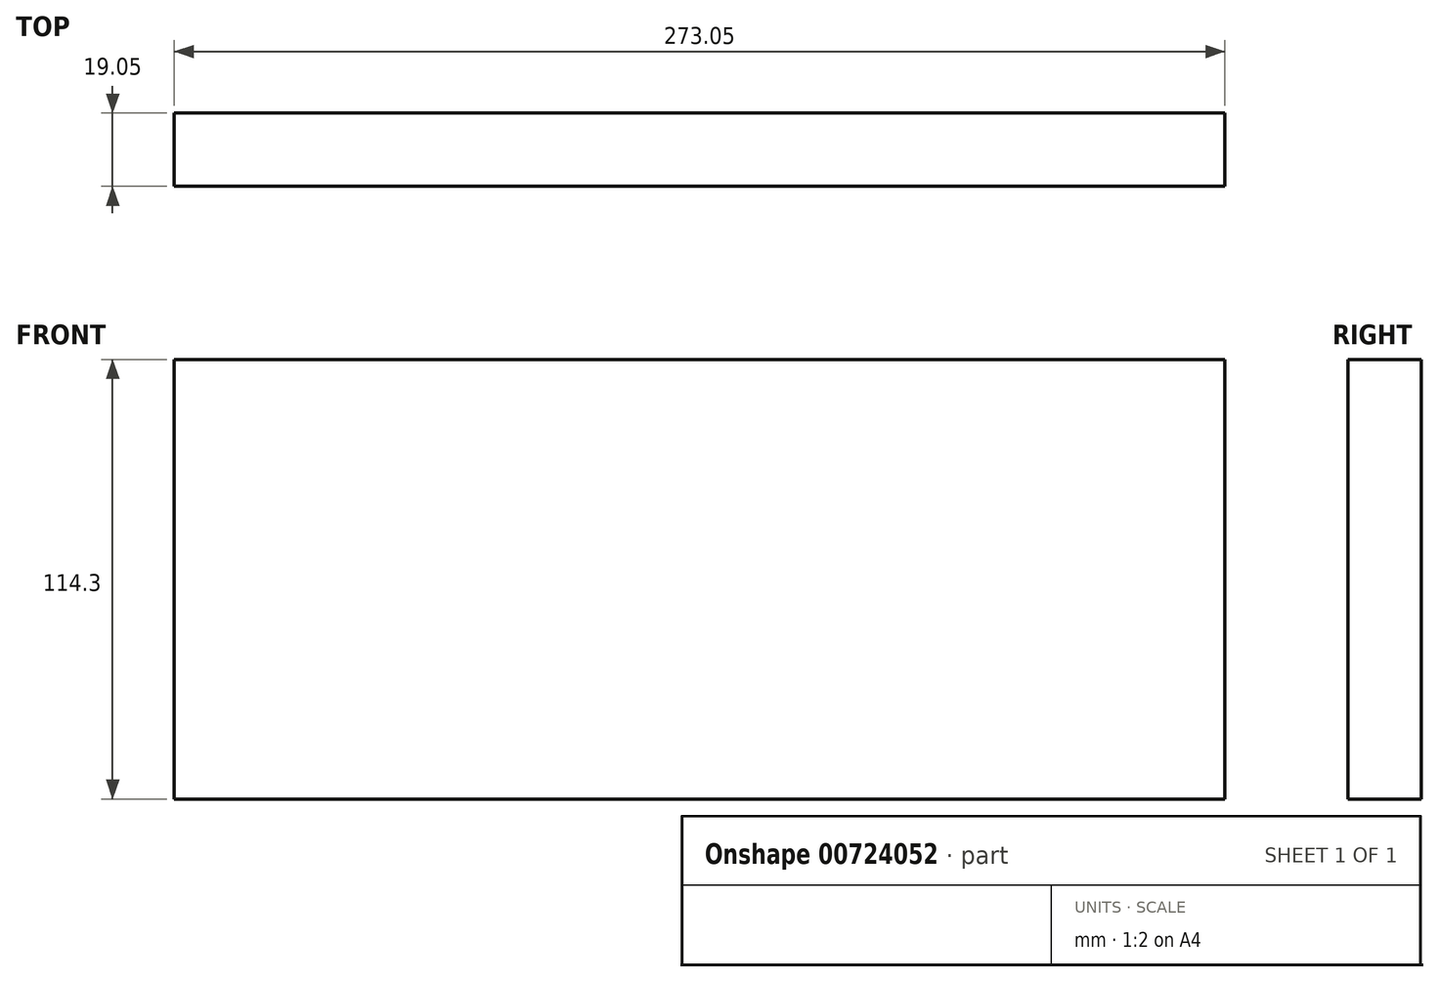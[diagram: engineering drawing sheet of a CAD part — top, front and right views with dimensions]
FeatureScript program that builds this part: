
annotation { "Feature Type Name" : "Feature", "Feature Type Description" : "" }
export const myFeature = defineFeature(function(context is Context, id is Id, definition is map)
    precondition{}
    {
        {
            var Q0;
            Q0=qCreatedBy(makeId("Front.planeOp"),FACE);
            var sketch = newSketch(context, id + "F0", { "sketchPlane" : qUnion([Q0])});
            skLineSegment(sketch, "E0.bottom", {"start": v(0, 0) * mm, "end": v(273.05, 0) * mm});
            skLineSegment(sketch, "E0.top", {"start": v(0, 114.3) * mm, "end": v(273.05, 114.3) * mm});
            skLineSegment(sketch, "E0.left", {"start": v(0, 0) * mm, "end": v(0, 114.3) * mm});
            skLineSegment(sketch, "E0.right", {"start": v(273.05, 0) * mm, "end": v(273.05, 114.3) * mm});
            skSolve(sketch);
        }
        {
            var Q0;
            Q0=makeQuery(id+"F0.imprint","IMPRINT",FACE,{"disambiguationData":[TD([[makeQuery(id+"F0.imprint","IMPRINT",EDGE,{"derivedFrom":sQuery(id+"F0.wireOp",EDGE,"E0.bottom")}),1.0]])]});
            extrude(context, id + "F1", {"entities" : qUnion([Q0]), "depth" : 19.05 * mm, "offsetDistance" : 25.4 * mm});
        }
        {
            var Q0;
            Q0=makeQuery(id+"F1.opExtrude","CAP_FACE",FACE,{"disambiguationData":[OSD([sQuery(id+"F0.wireOp",EDGE,"E0.bottom"),sQuery(id+"F0.wireOp",EDGE,"E0.top"),sQuery(id+"F0.wireOp",EDGE,"E0.left"),sQuery(id+"F0.wireOp",EDGE,"E0.right")])],"isStart":false});
            var sketch = newSketch(context, id + "F2", { "sketchPlane" : qUnion([Q0])});
            skLineSegment(sketch, "E1", {"start": v(63.12, 114.3) * mm, "end": v(63.12, 52.07) * mm});
            skLineSegment(sketch, "E2", {"start": v(63.12, 52.07) * mm, "end": v(110.07, 52.07) * mm});
            skLineSegment(sketch, "E3", {"start": v(110.07, 52.07) * mm, "end": v(110.07, 114.3) * mm});
            skSolve(sketch);
        }
    });
